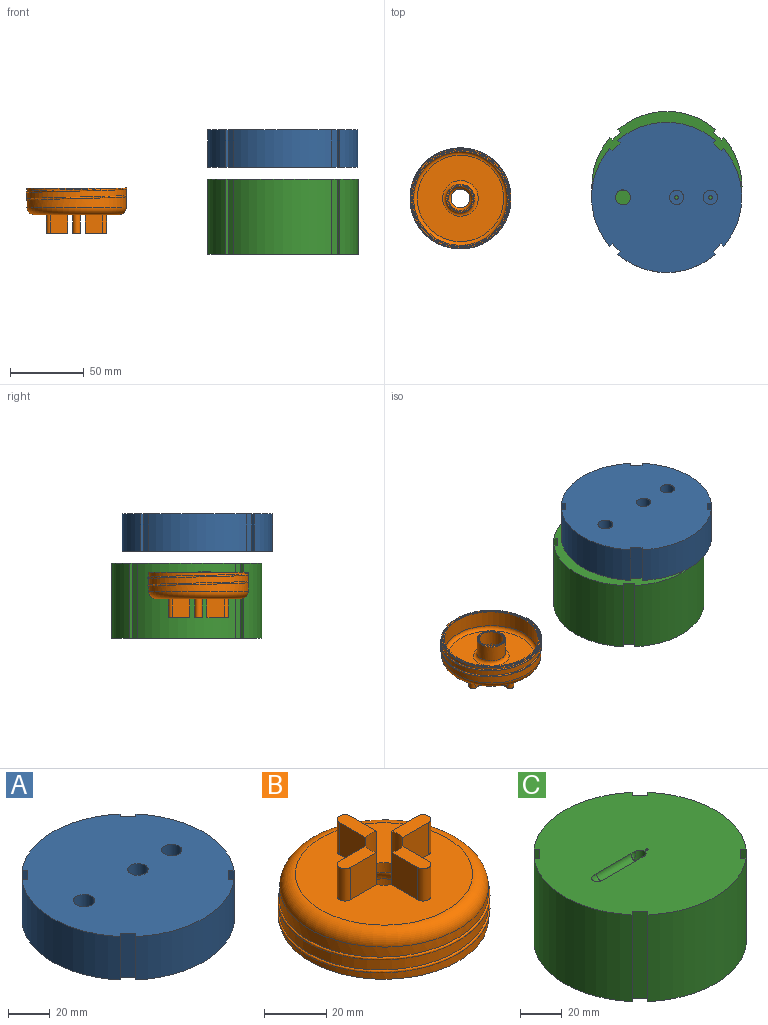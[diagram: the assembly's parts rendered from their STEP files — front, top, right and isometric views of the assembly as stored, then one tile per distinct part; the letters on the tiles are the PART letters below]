
ASSEMBLY  parts=3 mates=4
PART A: 31 faces, bbox 101.6x101.6x29.7 mm
  f0: cylinder r=1.27mm len=12.7mm, axis (0,0,1), area 101.3mm2, adj f6,f29
  f1: cylinder r=1.27mm len=12.7mm, axis (0,0,-1), area 101.3mm2, adj f6,f28
  f2: cylinder r=50.8mm len=66.25mm, axis (0,0,-1), area 1833.1mm2, adj f5,f6,f17,f19
  f3: cylinder r=50.8mm len=66.25mm, axis (0,0,-1), area 1833.1mm2, adj f5,f6,f14,f15
  f4: cylinder r=50.8mm len=66.25mm, axis (0,0,-1), area 1833.1mm2, adj f5,f6,f9,f12
  f5: plane 101.6x101.6mm, normal (0,0,1), area 7801.6mm2, adj f2,f3,f4,f7,f8,f9,f10,f11
  f6: plane 101.6x101.6mm, normal (0,0,-1), area 7656.5mm2, adj f0,f1,f2,f3,f4,f7,f8,f9
  f7: cylinder r=50.8mm len=66.25mm, axis (0,0,-1), area 1833.1mm2, adj f5,f6,f10,f18
  f8: cylinder r=5.08mm len=25.4mm, axis (0,0,1), area 734.1mm2, adj f5,f6,f23,f24,f25,f26
  f9: plane 25.4x1.7mm, normal (0.71,-0.71,0), area 60.9mm2, adj f4,f5,f6,f11
  f10: plane 25.4x1.7mm, normal (-0.71,0.71,0), area 60.9mm2, adj f5,f6,f7,f11
  f11: plane 25.4x5.39mm, normal (-0.71,-0.71,0), area 193.5mm2, adj f5,f6,f9,f10
  f12: plane 25.4x1.7mm, normal (0.71,0.71,0), area 60.9mm2, adj f4,f5,f6,f13
  f13: plane 25.4x5.39mm, normal (-0.71,0.71,0), area 193.5mm2, adj f5,f6,f12,f14
  f14: plane 25.4x1.7mm, normal (-0.71,-0.71,0), area 60.9mm2, adj f3,f5,f6,f13
  f15: plane 25.4x1.7mm, normal (0.71,-0.71,0), area 60.9mm2, adj f3,f5,f6,f16
  f16: plane 25.4x5.39mm, normal (0.71,0.71,0), area 193.5mm2, adj f5,f6,f15,f17
  f17: plane 25.4x1.7mm, normal (-0.71,0.71,0), area 60.9mm2, adj f2,f5,f6,f16
  f18: plane 25.4x1.7mm, normal (0.71,0.71,0), area 60.9mm2, adj f5,f6,f7,f20
  f19: plane 25.4x1.7mm, normal (-0.71,-0.71,0), area 60.9mm2, adj f2,f5,f6,f20
  f20: plane 25.4x5.39mm, normal (0.71,-0.71,0), area 193.5mm2, adj f5,f6,f18,f19
  f21: torus R=5.08mm, axis (0,-1,0), area 119.1mm2, adj f6,f22
  f22: cylinder r=5.08mm len=19.41mm, axis (-1,0,0), area 309.7mm2, adj f6,f21,f23,f24
  f23: torus R=5.08mm, axis (0,1,0), area 26.8mm2, adj f8,f22,f26
  f24: torus R=5.08mm, axis (0,1,0), area 26.8mm2, adj f8,f22,f25
  f25: cylinder r=5.08mm len=5.08mm, axis (1,0,0), area 2.2mm2, adj f6,f8,f24
  f26: cylinder r=5.08mm len=5.08mm, axis (1,0,0), area 2.2mm2, adj f6,f8,f23
  f27: cylinder r=4.86mm len=12.7mm, axis (0,0,1), area 388.1mm2, adj f5,f28
  f28: plane 9.73x9.73mm, normal (0,0,1), area 69.3mm2, adj f1,f27
  f29: plane 9.73x9.73mm, normal (0,0,1), area 69.3mm2, adj f0,f30
  f30: cylinder r=4.86mm len=12.7mm, axis (0,0,1), area 388.1mm2, adj f5,f29
PART B: 39 faces, bbox 73x80.2x31.1 mm
  f0: cylinder r=33.65mm len=67.31mm, axis (0,0,-1), area 966.8mm2, adj f1,f13,f33,f35
  f1: cylinder r=33.65mm len=67.31mm, axis (0,0,-1), area 859.2mm2, adj f0,f2,f35
  f2: cylinder r=33.65mm len=67.31mm, axis (0,0,-1), area 435.4mm2, adj f1,f3,f32,f35
  f3: plane 67.31x67.31mm, normal (0,0,-1), area 145.6mm2, adj f2,f31,f34
  f4: plane 64.89x64.89mm, normal (0,0,-1), area 140.3mm2, adj f11,f31
  f5: plane 19.05x19.05mm, normal (0,0,-1), area 22.3mm2, adj f29,f30
  f6: plane 17.27x17.27mm, normal (0,0,-1), area 20.2mm2, adj f28,f30
  f7: plane 14.5x5.08mm, normal (0,0,1), area 69.1mm2, adj f14,f24,f25,f27
  f8: plane 14.5x5.08mm, normal (0,0,1), area 69.1mm2, adj f15,f16,f17,f27
  f9: plane 14.5x5.08mm, normal (0,0,1), area 69.1mm2, adj f18,f19,f20,f27
  f10: plane 57.15x57.15mm, normal (0,0,1), area 2162.2mm2, adj f13,f14,f15,f16,f17,f18,f19,f20
  f11: cylinder r=31.75mm len=63.5mm, axis (0,0,-1), area 2280.2mm2, adj f4,f37
  f12: plane 58.42x58.42mm, normal (0,0,-1), area 2223.2mm2, adj f36,f37
  f13: torus R=28.57mm, axis (0,0,1), area 1594.8mm2, adj f0,f10
  f14: plane 12.7x11.96mm, normal (-1,0,0), area 151.9mm2, adj f7,f10,f25,f27
  f15: plane 12.7x11.96mm, normal (0,1,0), area 151.9mm2, adj f8,f10,f16,f27
  f16: cylinder r=2.54mm len=12.7mm, axis (0,0,-1), area 101.3mm2, adj f8,f10,f15,f17
  f17: plane 12.7x11.96mm, normal (0,-1,0), area 151.9mm2, adj f8,f10,f16,f27
  f18: plane 12.7x11.96mm, normal (-1,0,0), area 151.9mm2, adj f9,f10,f19,f27
  f19: cylinder r=2.54mm len=12.7mm, axis (0,0,-1), area 101.3mm2, adj f9,f10,f18,f20
  f20: plane 12.7x11.96mm, normal (1,0,0), area 151.9mm2, adj f9,f10,f19,f27
  f21: plane 12.7x11.96mm, normal (0,-1,0), area 151.9mm2, adj f10,f22,f26,f27
  f22: cylinder r=2.54mm len=12.7mm, axis (0,0,-1), area 101.3mm2, adj f10,f21,f23,f26
  f23: plane 12.7x11.96mm, normal (0,1,0), area 151.9mm2, adj f10,f22,f26,f27
  f24: plane 12.7x11.96mm, normal (1,0,0), area 151.9mm2, adj f7,f10,f25,f27
  f25: cylinder r=2.54mm len=12.7mm, axis (0,0,-1), area 101.3mm2, adj f7,f10,f14,f24
  f26: plane 14.5x5.08mm, normal (0,0,1), area 69.1mm2, adj f21,f22,f23,f27
  f27: cylinder r=6.35mm len=16.51mm, axis (0,0,1), area 417.5mm2, adj f7,f8,f9,f10,f14,f15,f17,f18
  f28: cylinder r=8.26mm len=16.51mm, axis (0,0,1), area 518.9mm2, adj f6,f38
  f29: cylinder r=9.53mm len=19.05mm, axis (0,0,1), area 684.1mm2, adj f5,f36
  f30: torus R=8.89mm, axis (0,0,-1), area 44.6mm2, adj f5,f6
  f31: torus R=32.7mm, axis (0,0,-1), area 165.7mm2, adj f3,f4
  f32: plane 1.16x0.65mm, normal (0,-1,0), area 0.4mm2, adj f2,f34,f35
  f33: plane 1.16x0.65mm, normal (0,1,0), area 0.4mm2, adj f0,f35
  f34: cylinder r=33.65mm len=19.66mm, axis (0,0,1), area 5.3mm2, adj f3,f32,f35
  f35: bspline ~80.07x69.34mm, area 681.5mm2, adj f0,f1,f2,f32,f33,f34
  f36: torus R=12.06mm, axis (0,0,1), area 261.9mm2, adj f12,f29
  f37: torus R=29.21mm, axis (0,0,1), area 772.8mm2, adj f11,f12
  f38: torus R=3.17mm, axis (0,0,1), area 217.3mm2, adj f27,f28
PART C: 45 faces, bbox 102.1x102.1x53.8 mm
  f0: cylinder r=43.43mm len=86.87mm, axis (0,0,1), area 1110.7mm2, adj f1,f2,f43,f44
  f1: bspline ~96.68x91.95mm, area 1284.8mm2, adj f0,f10,f42,f43,f44
  f2: bspline ~96.68x91.95mm, area 1285mm2, adj f0,f10,f42,f43,f44
  f3: cylinder r=50.8mm len=66.25mm, axis (0,0,1), area 3666.2mm2, adj f7,f8,f34,f35
  f4: cylinder r=50.8mm len=66.25mm, axis (0,0,1), area 3666.2mm2, adj f7,f8,f29,f37
  f5: cylinder r=50.8mm len=66.25mm, axis (0,0,1), area 3665.7mm2, adj f7,f8,f18,f19,f28,f32
  f6: cylinder r=50.8mm len=66.25mm, axis (0,0,1), area 3665.7mm2, adj f7,f8,f17,f18,f26,f31
  f7: plane 101.6x101.6mm, normal (0,0,-1), area 1043.6mm2, adj f3,f4,f5,f6,f10,f17,f19,f29
  f8: plane 102.05x102.05mm, normal (0,0,1), area 7836.9mm2, adj f3,f4,f5,f6,f14,f26,f27,f28
  f9: plane 67.34x67.34mm, normal (0,0,-1), area 3523mm2, adj f12,f15,f21,f41
  f10: cylinder r=45.97mm len=91.95mm, axis (0,0,1), area 10474.9mm2, adj f1,f2,f7,f11,f17,f18,f19,f42
  f11: plane 91.95x91.95mm, normal (0,0,-1), area 2375.7mm2, adj f10,f22
  f12: cylinder r=3.17mm len=6.35mm, axis (0,0,1), area 126.7mm2, adj f9,f13
  f13: plane 6.35x6.35mm, normal (0,0,-1), area 4.9mm2, adj f12,f14
  f14: cylinder r=2.92mm len=12.7mm, axis (0,0,-1), area 206.5mm2, adj f8,f13,f39
  f15: cylinder r=1.27mm len=12.7mm, axis (0,0,1), area 101.3mm2, adj f9,f16
  f16: plane 2.54x2.54mm, normal (0,0,-1), area 3.8mm2, adj f15,f20
  f17: plane 4.83x0.04mm, normal (0.28,0,0.96), area 0.2mm2, adj f6,f7,f10,f18
  f18: plane 50.8x50.8mm, normal (0,0,-1), area 347.8mm2, adj f5,f6,f10,f17,f19,f26,f27,f28
  f19: plane 4.83x0.01mm, normal (0,1,0), area 0.1mm2, adj f5,f7,f10,f18
  f20: cylinder r=0.64mm len=17.47mm, axis (0,0,-1), area 68.3mm2, adj f16,f40
  f21: cylinder r=33.67mm len=67.34mm, axis (0,0,1), area 1343.3mm2, adj f9,f24
  f22: cylinder r=36.84mm len=73.69mm, axis (0,0,1), area 1470mm2, adj f11,f25
  f23: plane 71.15x71.15mm, normal (0,0,-1), area 140.7mm2, adj f24,f25
  f24: torus R=34.94mm, axis (0,0,-1), area 427.8mm2, adj f21,f23
  f25: torus R=35.57mm, axis (0,0,-1), area 456mm2, adj f22,f23
  f26: plane 50.79x1.7mm, normal (0.71,-0.71,0), area 121.7mm2, adj f6,f8,f18,f27
  f27: plane 50.79x5.39mm, normal (0.71,0.71,0), area 387mm2, adj f8,f18,f26,f28
  f28: plane 50.79x1.7mm, normal (-0.71,0.71,0), area 121.7mm2, adj f5,f8,f18,f27
  f29: plane 50.8x1.7mm, normal (0.71,0.71,0), area 121.8mm2, adj f4,f7,f8,f30
  f30: plane 50.8x5.39mm, normal (-0.71,0.71,0), area 387.1mm2, adj f7,f8,f29,f31
  f31: plane 50.8x1.7mm, normal (-0.71,-0.71,0), area 121.8mm2, adj f6,f7,f8,f30
  f32: plane 50.8x1.7mm, normal (-0.71,-0.71,0), area 121.8mm2, adj f5,f7,f8,f33
  f33: plane 50.8x5.39mm, normal (0.71,-0.71,0), area 387.1mm2, adj f7,f8,f32,f34
  f34: plane 50.8x1.7mm, normal (0.71,0.71,0), area 121.8mm2, adj f3,f7,f8,f33
  f35: plane 50.8x1.7mm, normal (-0.71,0.71,0), area 121.8mm2, adj f3,f7,f8,f36
  f36: plane 50.8x5.39mm, normal (-0.71,-0.71,0), area 387.1mm2, adj f7,f8,f35,f37
  f37: plane 50.8x1.7mm, normal (0.71,-0.71,0), area 121.8mm2, adj f4,f7,f8,f36
  f38: cylinder r=2.92mm len=23.22mm, axis (-1,0,0), area 213.1mm2, adj f8,f39,f40
  f39: torus R=3.17mm, axis (0,-1,0), area 23.3mm2, adj f8,f14,f38
  f40: torus R=3.17mm, axis (0,1,0), area 38.8mm2, adj f8,f20,f38
  f41: cylinder r=0.64mm len=6.35mm, axis (0,0,-1), area 25.3mm2, adj f8,f9
  f42: plane 5.08x0.07mm, normal (1,0,0), area 0.4mm2, adj f1,f2,f10,f43
  f43: plane 5.01x2.54mm, normal (0.73,-0.69,0), area 13.1mm2, adj f0,f1,f2,f42
  f44: plane 5.08x1.95mm, normal (0.77,0.64,0), area 9.7mm2, adj f0,f1,f2,f10
PLACE A t=(-28.68,-24.9,38.86)mm
PLACE B rot(axis=(1,0,0),180deg) t=(-168.16,-25.51,24.61)mm
PLACE C t=(-28.5,-17.52,7.45)mm
MATE parallel A.f6 <-> C.f8  axis (0,0,-1) through (-27.96,-24.9,38.86)mm
MATE parallel A.f9 <-> C.f37  axis (0.71,-0.71,0) through (-65.5,-56.33,38.86)mm
MATE parallel A.f11 <-> C.f36  axis (-0.71,-0.71,0) through (-65.5,-56.33,38.86)mm
MATE parallel B.f11 <-> C.f9  axis (0,0,1) through (-168.16,-25.51,24.61)mm
